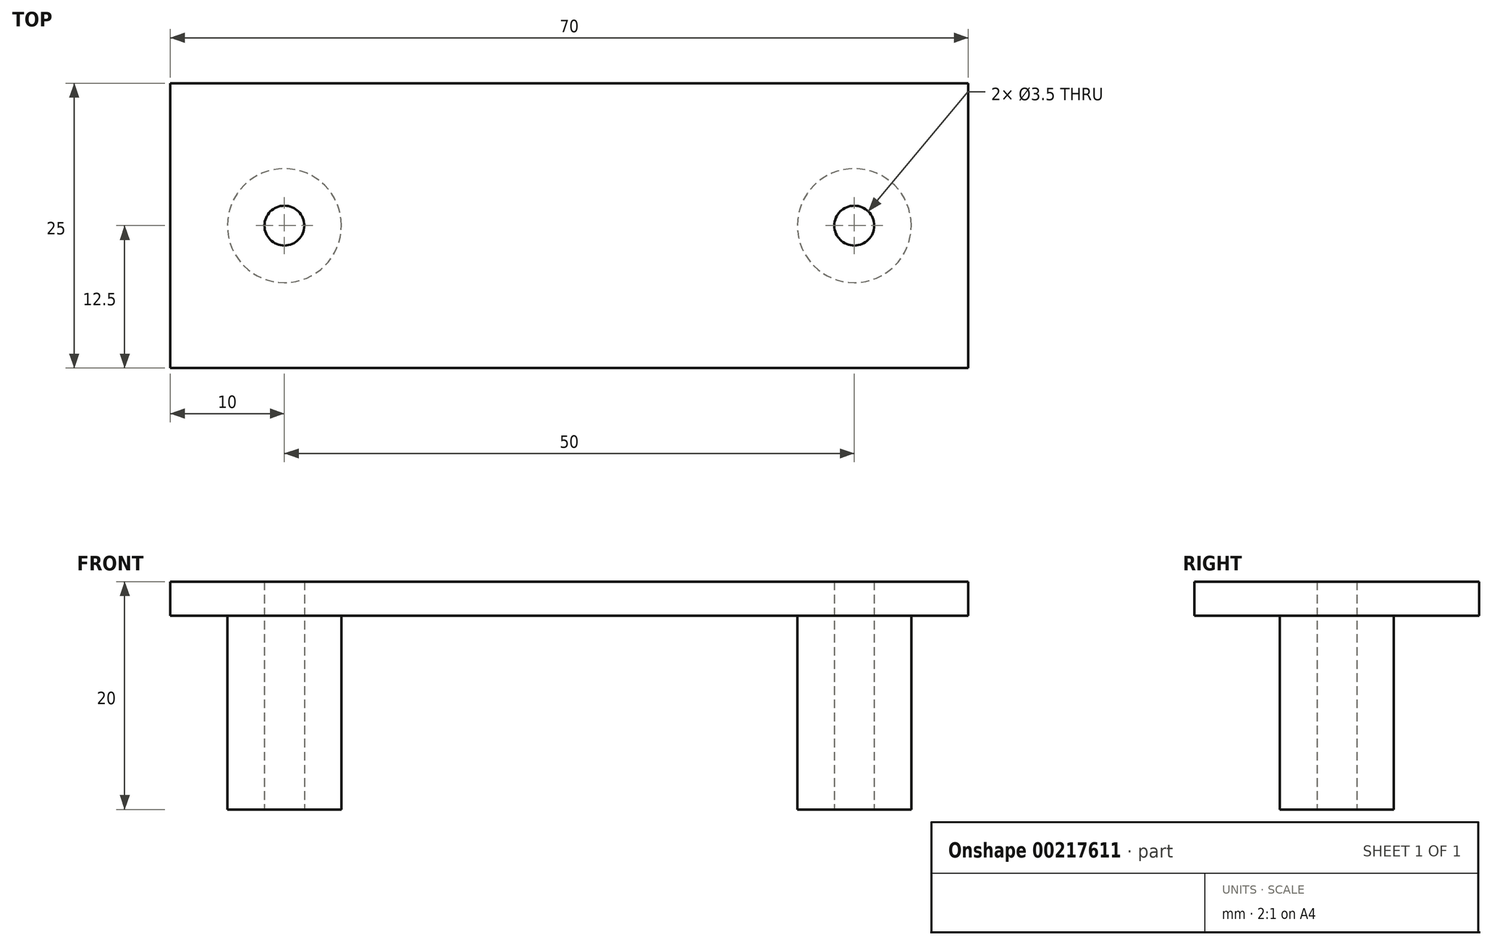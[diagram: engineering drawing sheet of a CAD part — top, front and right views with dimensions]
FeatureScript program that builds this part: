
annotation { "Feature Type Name" : "Feature", "Feature Type Description" : "" }
export const myFeature = defineFeature(function(context is Context, id is Id, definition is map)
    precondition{}
    {
        {
            var Q0;
            Q0=qCreatedBy(makeId("Top.planeOp"),FACE);
            var sketch = newSketch(context, id + "F0", { "sketchPlane" : qUnion([Q0])});
            skLineSegment(sketch, "E0", {"start": v(0, 39.27) * mm, "end": v(0, -28.86) * mm, "construction": true});
            skLineSegment(sketch, "E1", {"start": v(0, 0) * mm, "end": v(29.18, 0) * mm});
            skLineSegment(sketch, "E2.bottom", {"start": v(-35, 12.5) * mm, "end": v(35, 12.5) * mm});
            skLineSegment(sketch, "E2.top", {"start": v(-35, -12.5) * mm, "end": v(35, -12.5) * mm});
            skLineSegment(sketch, "E2.left", {"start": v(-35, 12.5) * mm, "end": v(-35, -12.5) * mm});
            skLineSegment(sketch, "E2.right", {"start": v(35, 12.5) * mm, "end": v(35, -12.5) * mm});
            skCircle(sketch, "E3", {"center": v(-25, 0) * mm, "radius": 1.75 * mm});
            skCircle(sketch, "E4", {"center": v(25, 0) * mm, "radius": 1.75 * mm});
            skSolve(sketch);
        }
        {
            var Q0;
            Q0=makeQuery(id+"F0.imprint","IMPRINT",FACE,{"disambiguationData":[TD([[makeQuery(id+"F0.imprint","IMPRINT",EDGE,{"derivedFrom":sQuery(id+"F0.wireOp",EDGE,"E2.bottom")}),-1.0]])]});
            extrude(context, id + "F1", {"entities" : qUnion([Q0]), "depth" : 3 * mm});
        }
        {
            var Q0;
            Q0=makeQuery(id+"F1.opExtrude","CAP_FACE",FACE,{"disambiguationData":[OSD([sQuery(id+"F0.wireOp",EDGE,"E2.bottom"),sQuery(id+"F0.wireOp",EDGE,"E2.top"),sQuery(id+"F0.wireOp",EDGE,"E2.left"),sQuery(id+"F0.wireOp",EDGE,"E2.right"),sQuery(id+"F0.wireOp",EDGE,"E3"),sQuery(id+"F0.wireOp",EDGE,"E4")])],"isStart":false});
            var sketch = newSketch(context, id + "F2", { "sketchPlane" : qUnion([Q0])});
            skCircle(sketch, "E5", {"center": v(-25, 0) * mm, "radius": 5 * mm});
            skCircle(sketch, "E6", {"center": v(25, 0) * mm, "radius": 5 * mm});
            skCircle(sketch, "E7.0", {"center": v(25, 0) * mm, "radius": 1.75 * mm});
            skCircle(sketch, "E8.0", {"center": v(-25, 0) * mm, "radius": 1.75 * mm});
            skSolve(sketch);
        }
        {
            var Q0;
            Q0=qSketchRegion(id+"F2",true);
            extrude(context, id + "F3", {"entities" : qUnion([Q0]), "operationType" : NewBodyOperationType.ADD, "oppositeDirection" : true, "depth" : 20 * mm});
        }
    });
